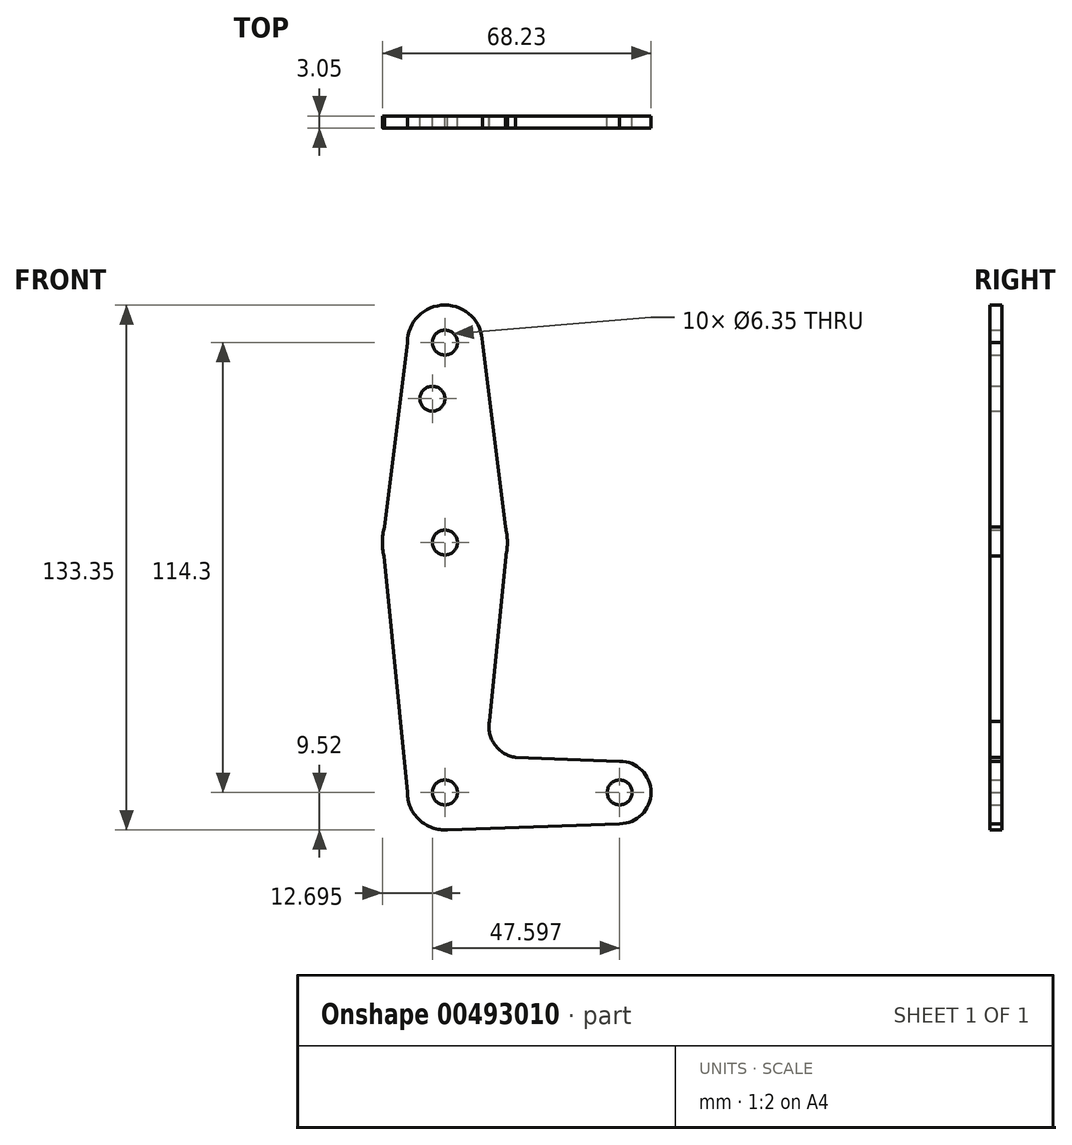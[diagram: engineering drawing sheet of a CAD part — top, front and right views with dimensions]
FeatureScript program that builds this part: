
annotation { "Feature Type Name" : "Feature", "Feature Type Description" : "" }
export const myFeature = defineFeature(function(context is Context, id is Id, definition is map)
    precondition{}
    {
        {
            var Q0;
            Q0=qCreatedBy(makeId("Front.planeOp"),FACE);
            var sketch = newSketch(context, id + "F0", { "sketchPlane" : qUnion([Q0])});
            skCircle(sketch, "E0", {"center": v(0, 114.3) * mm, "radius": 9.53 * mm});
            skCircle(sketch, "E1", {"center": v(0, 0) * mm, "radius": 9.53 * mm});
            skCircle(sketch, "E2", {"center": v(44.42, 0) * mm, "radius": 7.94 * mm});
            skCircle(sketch, "E3", {"center": v(0, 63.5) * mm, "radius": 15.88 * mm});
            skLineSegment(sketch, "E4", {"start": v(9.53, 114.3) * mm, "end": v(15.88, 63.5) * mm});
            skLineSegment(sketch, "E5", {"start": v(-9.52, 114.3) * mm, "end": v(-15.87, 63.5) * mm});
            skLineSegment(sketch, "E6", {"start": v(-15.5, 60.04) * mm, "end": v(-9.53, 0) * mm});
            skCircle(sketch, "E7", {"center": v(0, 114.3) * mm, "radius": 3.18 * mm});
            skLineSegment(sketch, "E8", {"start": v(44.42, 0) * mm, "end": v(0, 0) * mm, "construction": true});
            skLineSegment(sketch, "E9", {"start": v(0, -9.53) * mm, "end": v(44.42, -7.94) * mm});
            skLineSegment(sketch, "E10", {"start": v(44.42, -7.94) * mm, "end": v(0, -9.52) * mm});
            skArc(sketch, "E11", {"start": v(11.32, 18.08) * mm, "mid": v(12.7, 12.1) * mm, "end": v(17.93, 8.88) * mm});
            skCircle(sketch, "E12", {"center": v(0, 63.5) * mm, "radius": 3.18 * mm});
            skCircle(sketch, "E13", {"center": v(0, 0) * mm, "radius": 3.18 * mm});
            skCircle(sketch, "E14", {"center": v(-3.18, 100.03) * mm, "radius": 3.18 * mm});
            skLineSegment(sketch, "E15", {"start": v(0, 114.3) * mm, "end": v(0, 0) * mm, "construction": true});
            skCircle(sketch, "E16", {"center": v(44.42, 0) * mm, "radius": 3.18 * mm});
            skLineSegment(sketch, "E17", {"start": v(15.5, 60.04) * mm, "end": v(11.32, 18.08) * mm});
            skLineSegment(sketch, "E18", {"start": v(17.93, 8.88) * mm, "end": v(44.42, 7.94) * mm});
            skSolve(sketch);
        }
        {
            var Q0;
            Q0 = qSketchRegion(id + "F0", true);
            extrude(context, id + "F1", {"entities" : qUnion([Q0]), "depth" : 3.05 * mm, "offsetDistance" : 25.4 * mm});
        }
    });
